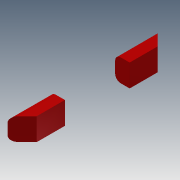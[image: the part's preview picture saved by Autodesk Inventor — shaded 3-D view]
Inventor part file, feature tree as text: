
AUTODESK INVENTOR PART (.ipt)
format: ipt  version: 2014 (Build 180170000, 170)  size: 107,008 bytes
history: native  units: in
note: dims shown in document units (in); Inventor stores cm internally (conversion verified against a paired STEP export)
features: extrude x3, sketch x3
ambient origin geometry x8: Origin, YZ Plane, XZ Plane, XY Plane, X Axis, Y Axis, Z Axis, Center Point
bodies: Solid1 (feature_tree)
feature tree (6):
  extrude  "Extrusion1"  Depth=5.0in
  extrude  "Extrusion2"  Depth=2.5in
  extrude  "Extrusion3"  Depth=5.0in TaperAngle=0.0deg
  sketch  "Sketch1"  dims[d0=0.75in d1=5.0in]
  sketch  "Sketch2"  dims[d2=2.5in d3=2.5in]
  sketch  "Sketch3"  dims[d4=1.25in d5=33.5in d6=0.0in d8=45.0deg d10=45.0deg d11=5.0in d12=0.0in d13=14.45in d14=5.0in d15=0.0in]
